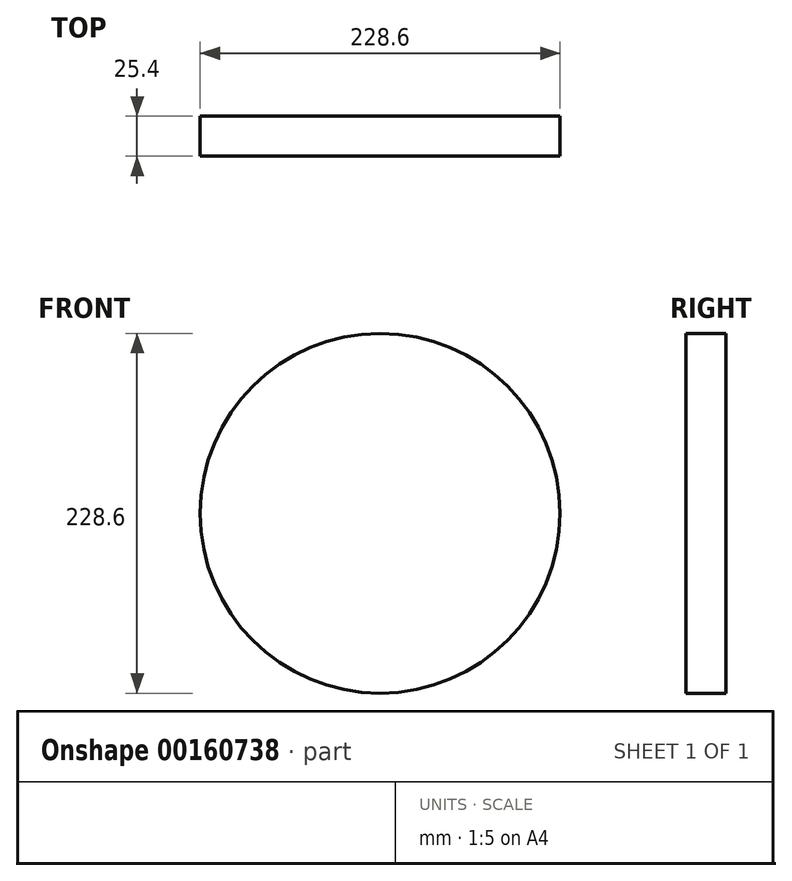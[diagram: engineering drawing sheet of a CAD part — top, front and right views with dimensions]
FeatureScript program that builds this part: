
annotation { "Feature Type Name" : "Feature", "Feature Type Description" : "" }
export const myFeature = defineFeature(function(context is Context, id is Id, definition is map)
    precondition{}
    {
        {
            var Q0;
            Q0=qCreatedBy(makeId("Front.planeOp"),FACE);
            var sketch = newSketch(context, id + "F0", { "sketchPlane" : qUnion([Q0])});
            skCircle(sketch, "E0", {"center": v(0, 0) * mm, "radius": 114.3 * mm});
            skSolve(sketch);
        }
        {
            var Q0;
            Q0 = qSketchRegion(id + "F0", true);
            extrude(context, id + "F1", {"entities" : qUnion([Q0]), "depth" : 25.4 * mm});
        }
    });
